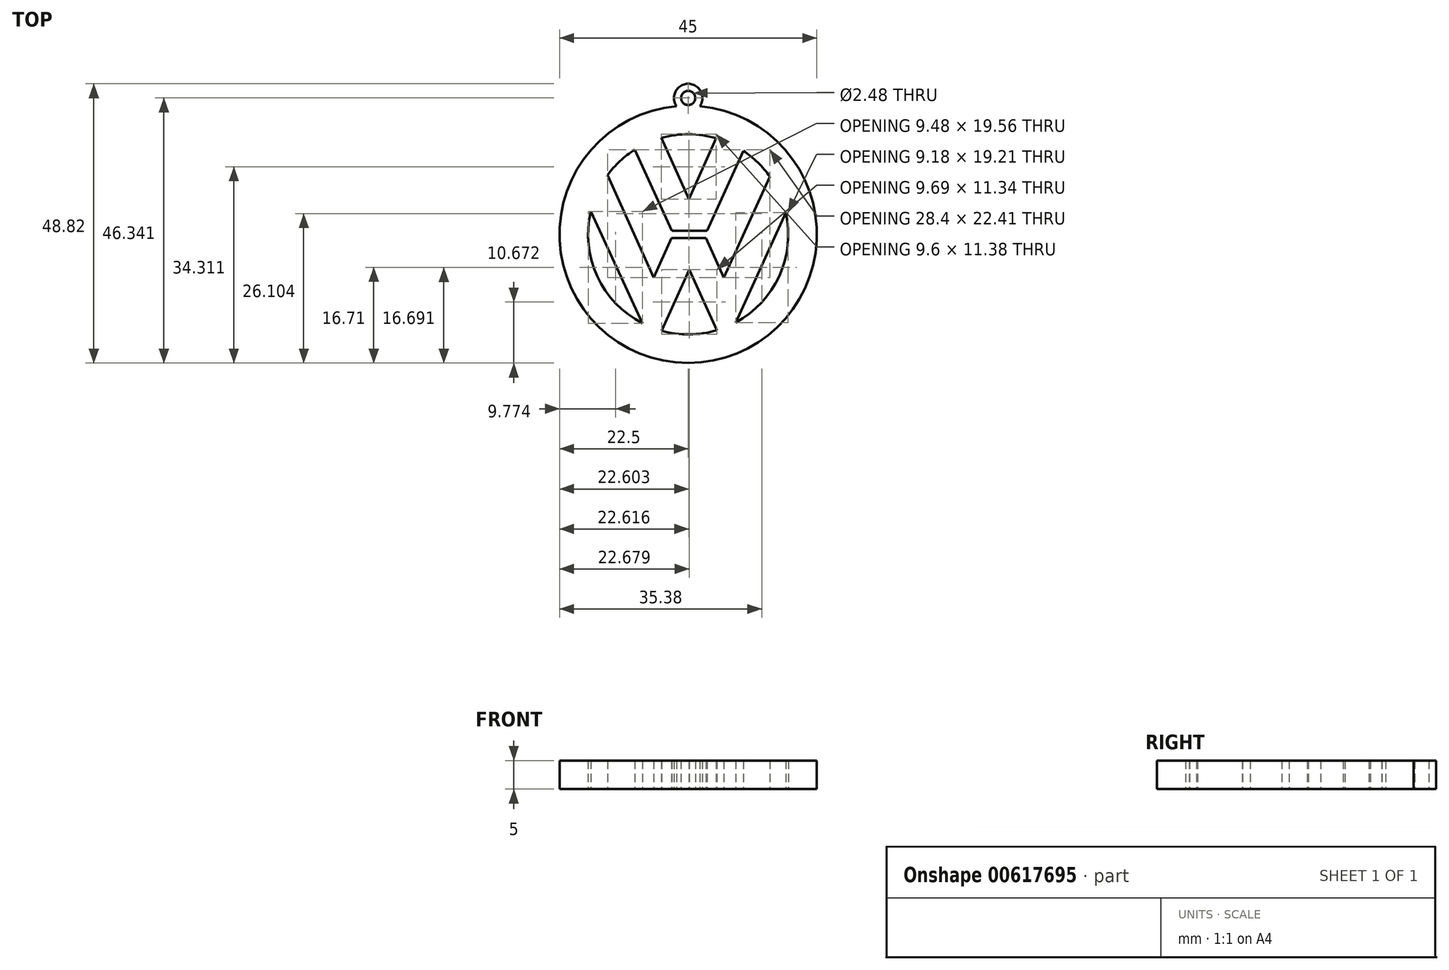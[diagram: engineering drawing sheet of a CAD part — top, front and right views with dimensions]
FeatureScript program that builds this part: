
annotation { "Feature Type Name" : "Feature", "Feature Type Description" : "" }
export const myFeature = defineFeature(function(context is Context, id is Id, definition is map)
    precondition{}
    {
        {
            var Q0;
            Q0=qCreatedBy(makeId("Top.planeOp"),FACE);
            var sketch = newSketch(context, id + "F0", { "sketchPlane" : qUnion([Q0])});
            skArc(sketch, "E0", {"start": v(-2.03, 22.4) * mm, "mid": v(0, -22.5) * mm, "end": v(2.03, 22.4) * mm});
            skArc(sketch, "E1", {"start": v(-17.04, 4) * mm, "mid": v(-15.88, -7.35) * mm, "end": v(-7.99, -15.57) * mm});
            skLineSegment(sketch, "E2", {"start": v(4.91, 16.8) * mm, "end": v(0.11, 6.12) * mm});
            skLineSegment(sketch, "E3", {"start": v(9.63, 14.6) * mm, "end": v(3.28, 0.62) * mm});
            skLineSegment(sketch, "E4", {"start": v(14.3, 10.08) * mm, "end": v(6.23, -7.6) * mm});
            skLineSegment(sketch, "E5", {"start": v(17.08, 3.8) * mm, "end": v(8.29, -15.41) * mm});
            skLineSegment(sketch, "E6", {"start": v(-17.04, 4) * mm, "end": v(-7.99, -15.57) * mm});
            skLineSegment(sketch, "E7", {"start": v(-14.1, 10.37) * mm, "end": v(-6.04, -7.54) * mm});
            skLineSegment(sketch, "E8", {"start": v(-9.33, 14.8) * mm, "end": v(-2.88, 0.62) * mm});
            skLineSegment(sketch, "E9", {"start": v(-4.68, 16.86) * mm, "end": v(0.11, 6.12) * mm});
            skLineSegment(sketch, "E10", {"start": v(-2.88, 0.62) * mm, "end": v(3.28, 0.62) * mm});
            skLineSegment(sketch, "E11", {"start": v(-2.94, -0.65) * mm, "end": v(3.13, -0.65) * mm});
            skArc(sketch, "E12.trimOffspring", {"start": v(-9.33, 14.8) * mm, "mid": v(-11.92, 12.81) * mm, "end": v(-14.1, 10.37) * mm});
            skArc(sketch, "E13.trimOffspring", {"start": v(4.91, 16.8) * mm, "mid": v(0.12, 17.5) * mm, "end": v(-4.68, 16.86) * mm});
            skArc(sketch, "E14.trimOffspring", {"start": v(14.3, 10.08) * mm, "mid": v(12.18, 12.56) * mm, "end": v(9.63, 14.6) * mm});
            skArc(sketch, "E15.trimOffspring", {"start": v(8.29, -15.41) * mm, "mid": v(15.91, -7.29) * mm, "end": v(17.08, 3.8) * mm});
            skArc(sketch, "E16.trimOffspring", {"start": v(-4.66, -16.87) * mm, "mid": v(0.19, -17.5) * mm, "end": v(5.02, -16.76) * mm});
            skLineSegment(sketch, "E17.trimOffspring", {"start": v(0.2, -6.16) * mm, "end": v(5.02, -16.76) * mm});
            skLineSegment(sketch, "E18.trimOffspring", {"start": v(-2.94, -0.65) * mm, "end": v(-6.04, -7.54) * mm});
            skLineSegment(sketch, "E19.trimOffspring", {"start": v(0.2, -6.16) * mm, "end": v(-4.66, -16.87) * mm});
            skLineSegment(sketch, "E20.trimOffspring", {"start": v(3.13, -0.65) * mm, "end": v(6.23, -7.6) * mm});
            skCircle(sketch, "E21", {"center": v(0, 23.84) * mm, "radius": 1.24 * mm});
            skArc(sketch, "E22", {"start": v(2.03, 22.4) * mm, "mid": v(0, 26.32) * mm, "end": v(-2.03, 22.4) * mm});
            skSolve(sketch);
        }
        {
            var Q0;
            Q0 = qSketchRegion(id + "F0", true);
            extrude(context, id + "F1", {"entities" : qUnion([Q0]), "depth" : 5 * mm, "offsetDistance" : 25 * mm});
        }
    });
